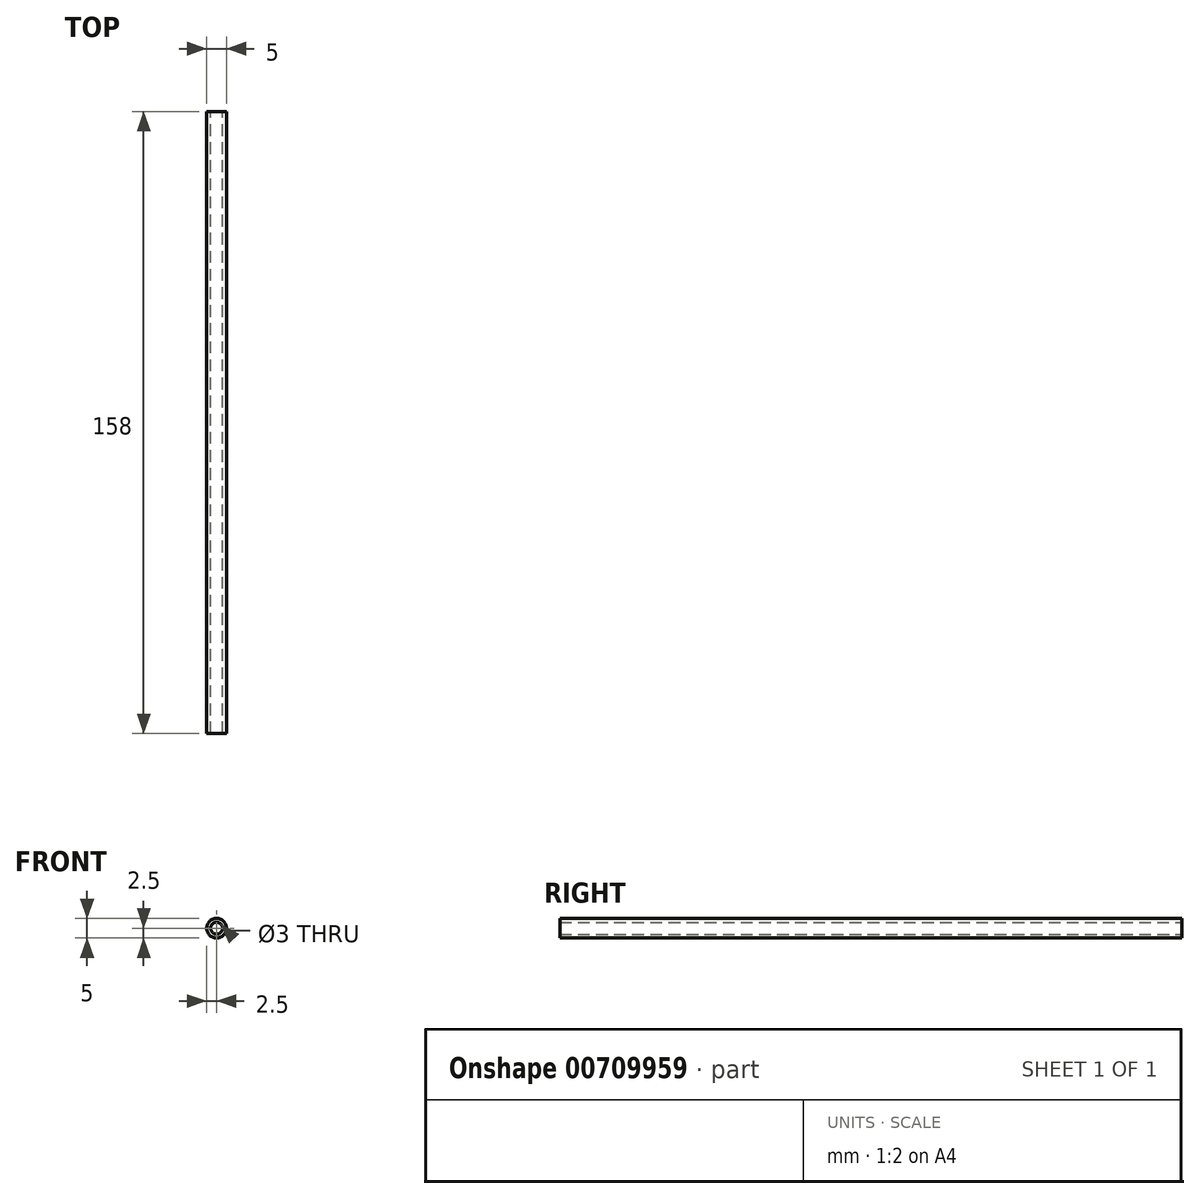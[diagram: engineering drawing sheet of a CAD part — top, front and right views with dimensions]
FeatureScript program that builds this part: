
annotation { "Feature Type Name" : "Feature", "Feature Type Description" : "" }
export const myFeature = defineFeature(function(context is Context, id is Id, definition is map)
    precondition{}
    {
        {
            var Q0;
            Q0=qCreatedBy(makeId("Front.planeOp"),FACE);
            var sketch = newSketch(context, id + "F0", { "sketchPlane" : qUnion([Q0])});
            skCircle(sketch, "E0", {"center": v(0, 0) * mm, "radius": 2.5 * mm});
            skCircle(sketch, "E1", {"center": v(0, 0) * mm, "radius": 1.5 * mm});
            skSolve(sketch);
        }
        {
            var Q0;
            Q0=makeQuery(id+"F0.imprint","IMPRINT",FACE,{"disambiguationData":[TD([[makeQuery(id+"F0.imprint","IMPRINT",EDGE,{"derivedFrom":sQuery(id+"F0.wireOp",EDGE,"E0")}),1.0]])]});
            extrude(context, id + "F1", {"entities" : qUnion([Q0]), "endBound" : BoundingType.SYMMETRIC, "depth" : 158 * mm, "offsetDistance" : 25 * mm});
        }
    });
